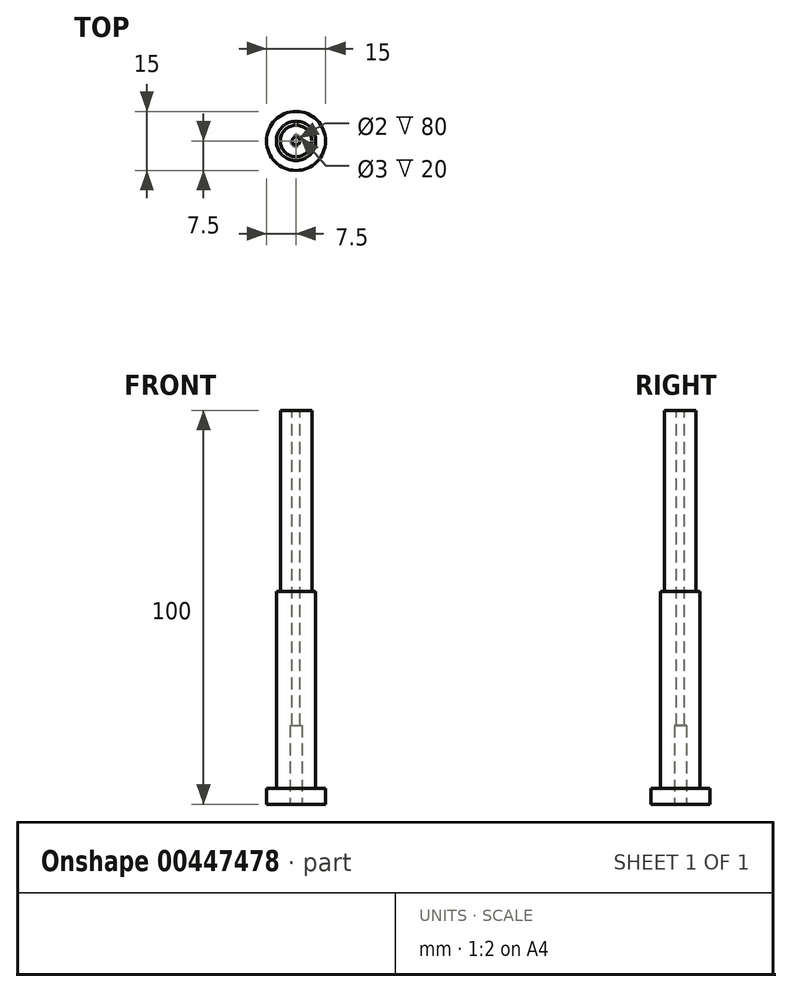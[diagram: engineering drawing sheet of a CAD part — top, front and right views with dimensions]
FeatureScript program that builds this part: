
annotation { "Feature Type Name" : "Feature", "Feature Type Description" : "" }
export const myFeature = defineFeature(function(context is Context, id is Id, definition is map)
    precondition{}
    {
        {
            var Q0;
            Q0=qCreatedBy(makeId("Top.planeOp"),FACE);
            var sketch = newSketch(context, id + "F0", { "sketchPlane" : qUnion([Q0])});
            skCircle(sketch, "E0", {"center": v(0, 0) * mm, "radius": 7.5 * mm});
            skSolve(sketch);
        }
        {
            var Q0;
            Q0=qSketchRegion(id+"F0",true);
            extrude(context, id + "F1", {"entities" : qUnion([Q0]), "depth" : 4 * mm});
        }
        {
            var Q0;
            Q0=qCreatedBy(makeId("Top.planeOp"),FACE);
            var sketch = newSketch(context, id + "F2", { "sketchPlane" : qUnion([Q0])});
            skCircle(sketch, "E1", {"center": v(0, 0) * mm, "radius": 5 * mm});
            skSolve(sketch);
        }
        {
            var Q0;
            Q0=qSketchRegion(id+"F2",true);
            extrude(context, id + "F3", {"entities" : qUnion([Q0]), "operationType" : NewBodyOperationType.ADD, "depth" : 54 * mm});
        }
        {
            var Q0;
            Q0=makeQuery(id+"F3.opExtrude","CAP_FACE",FACE,{"disambiguationData":[OSD([sQuery(id+"F2.wireOp",EDGE,"E1")])],"isStart":false});
            var sketch = newSketch(context, id + "F4", { "sketchPlane" : qUnion([Q0])});
            skCircle(sketch, "E2", {"center": v(0, 0) * mm, "radius": 4 * mm});
            skSolve(sketch);
        }
        {
            var Q0;
            Q0=makeQuery(id+"F4.imprint","IMPRINT",FACE,{"disambiguationData":[TD([[makeQuery(id+"F4.imprint","IMPRINT",EDGE,{"derivedFrom":sQuery(id+"F4.wireOp",EDGE,"E2")}),1.0]])]});
            extrude(context, id + "F5", {"entities" : qUnion([Q0]), "operationType" : NewBodyOperationType.ADD, "depth" : 46 * mm});
        }
        {
            var Q0;
            Q0=makeQuery(id+"F5.opExtrude","CAP_FACE",FACE,{"disambiguationData":[OSD([sQuery(id+"F4.wireOp",EDGE,"E2")])],"isStart":false});
            var sketch = newSketch(context, id + "F6", { "sketchPlane" : qUnion([Q0])});
            skCircle(sketch, "E3", {"center": v(0, 0) * mm, "radius": 1 * mm});
            skSolve(sketch);
        }
        {
            var Q0;
            Q0 = qSketchRegion(id + "F6", true);
            extrude(context, id + "F7", {"entities" : qUnion([Q0]), "operationType" : NewBodyOperationType.REMOVE, "oppositeDirection" : true, "depth" : 120 * mm});
        }
        {
            var Q0;
            Q0=makeQuery(id+"F1.opExtrude","CAP_FACE",FACE,{"disambiguationData":[OSD([sQuery(id+"F0.wireOp",EDGE,"E0")])],"isStart":true});
            var sketch = newSketch(context, id + "F8", { "sketchPlane" : qUnion([Q0])});
            skCircle(sketch, "E4", {"center": v(0, 0) * mm, "radius": 1.5 * mm});
            skSolve(sketch);
        }
        {
            var Q0;
            Q0 = qSketchRegion(id + "F8", true);
            extrude(context, id + "F9", {"entities" : qUnion([Q0]), "operationType" : NewBodyOperationType.REMOVE, "oppositeDirection" : true, "depth" : 20 * mm});
        }
    });
